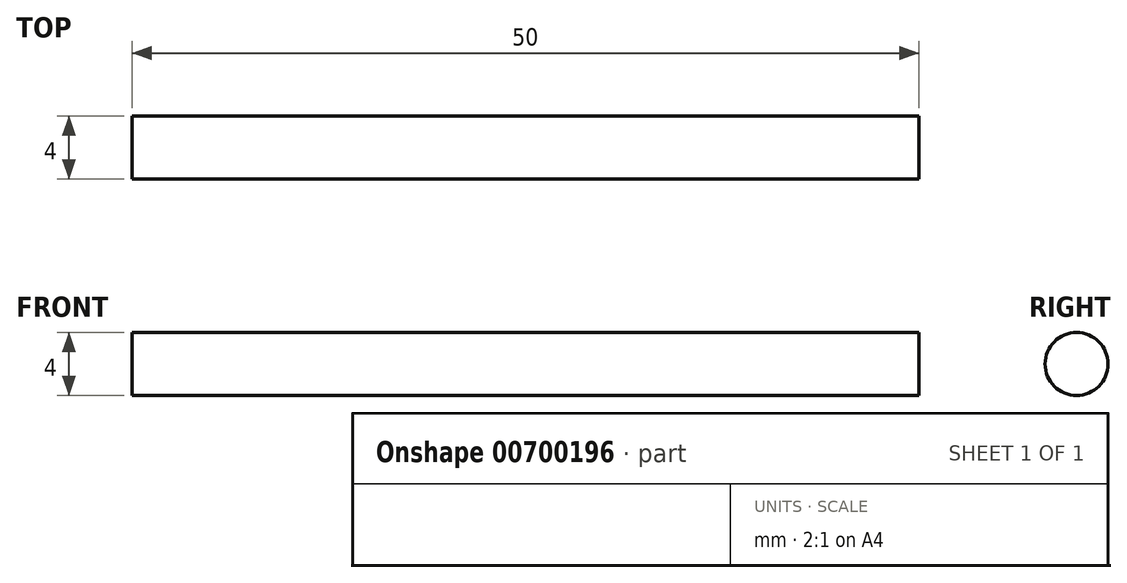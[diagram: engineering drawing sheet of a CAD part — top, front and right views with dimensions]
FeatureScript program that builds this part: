
annotation { "Feature Type Name" : "Feature", "Feature Type Description" : "" }
export const myFeature = defineFeature(function(context is Context, id is Id, definition is map)
    precondition{}
    {
        {
            var Q0;
            Q0=qCreatedBy(makeId("Right.planeOp"),FACE);
            var sketch = newSketch(context, id + "F0", { "sketchPlane" : qUnion([Q0])});
            skCircle(sketch, "E0", {"center": v(0, 0) * mm, "radius": 2 * mm});
            skSolve(sketch);
        }
        {
            var Q0;
            Q0=qSketchRegion(id+"F0",true);
            extrude(context, id + "F1", {"entities" : qUnion([Q0]), "depth" : 50 * mm, "offsetDistance" : 25 * mm});
        }
    });
